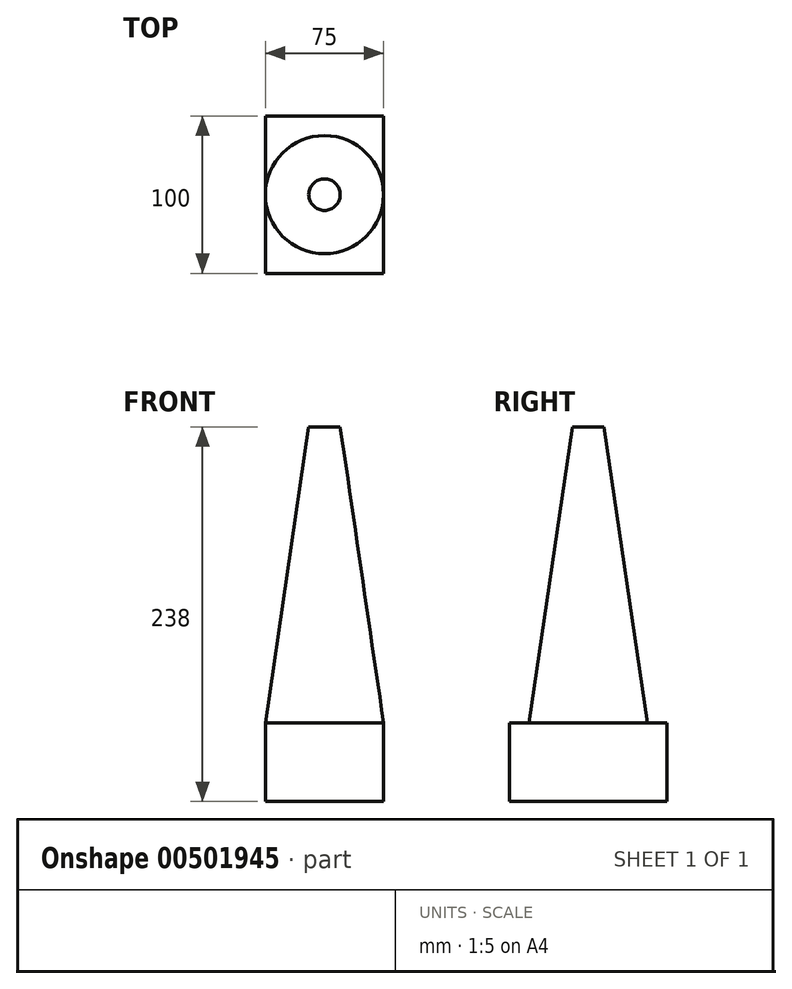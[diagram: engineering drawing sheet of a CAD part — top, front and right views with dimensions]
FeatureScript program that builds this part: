
annotation { "Feature Type Name" : "Feature", "Feature Type Description" : "" }
export const myFeature = defineFeature(function(context is Context, id is Id, definition is map)
    precondition{}
    {
        {
            var Q0;
            Q0=qCreatedBy(makeId("Top.planeOp"),FACE);
            var sketch = newSketch(context, id + "F0", { "sketchPlane" : qUnion([Q0])});
            skLineSegment(sketch, "E0.bottom", {"start": v(37.5, -50) * mm, "end": v(-37.5, -50) * mm});
            skLineSegment(sketch, "E0.top", {"start": v(37.5, 50) * mm, "end": v(-37.5, 50) * mm});
            skLineSegment(sketch, "E0.left", {"start": v(37.5, -50) * mm, "end": v(37.5, 50) * mm});
            skLineSegment(sketch, "E0.right", {"start": v(-37.5, -50) * mm, "end": v(-37.5, 50) * mm});
            skPoint(sketch, "E0.middle", {"position": v(0, 0) * mm});
            skSolve(sketch);
        }
        {
            var Q0;
            Q0=makeQuery(id+"F0.imprint","IMPRINT",FACE,{"disambiguationData":[TD([[makeQuery(id+"F0.imprint","IMPRINT",EDGE,{"derivedFrom":sQuery(id+"F0.wireOp",EDGE,"E0.bottom")}),-1.0]])]});
            extrude(context, id + "F1", {"entities" : qUnion([Q0]), "oppositeDirection" : true, "depth" : 50 * mm});
        }
        {
            var Q0;
            Q0=qCreatedBy(makeId("Right.planeOp"),FACE);
            var sketch = newSketch(context, id + "F2", { "sketchPlane" : qUnion([Q0])});
            skLineSegment(sketch, "E1", {"start": v(0, 188) * mm, "end": v(0, 0) * mm});
            skLineSegment(sketch, "E2", {"start": v(0, 0) * mm, "end": v(-37.5, 0) * mm});
            skLineSegment(sketch, "E3", {"start": v(-37.5, 0) * mm, "end": v(-10, 188) * mm});
            skLineSegment(sketch, "E4", {"start": v(-10, 188) * mm, "end": v(0, 188) * mm});
            skSolve(sketch);
        }
        {
            var Q0;
            Q0=makeQuery(id+"F2.imprint","IMPRINT",FACE,{"disambiguationData":[TD([[makeQuery(id+"F2.imprint","IMPRINT",EDGE,{"derivedFrom":sQuery(id+"F2.wireOp",EDGE,"E1")}),-1.0]])]});
            var Q1;
            Q1=sQuery(id+"F2.wireOp",EDGE,"E1");
            revolve(context, id + "F3", {"operationType" : NewBodyOperationType.ADD, "entities" : qUnion([Q0]), "axis" : qUnion([Q1]), "revolveType" : RevolveType.FULL});
        }
    });
